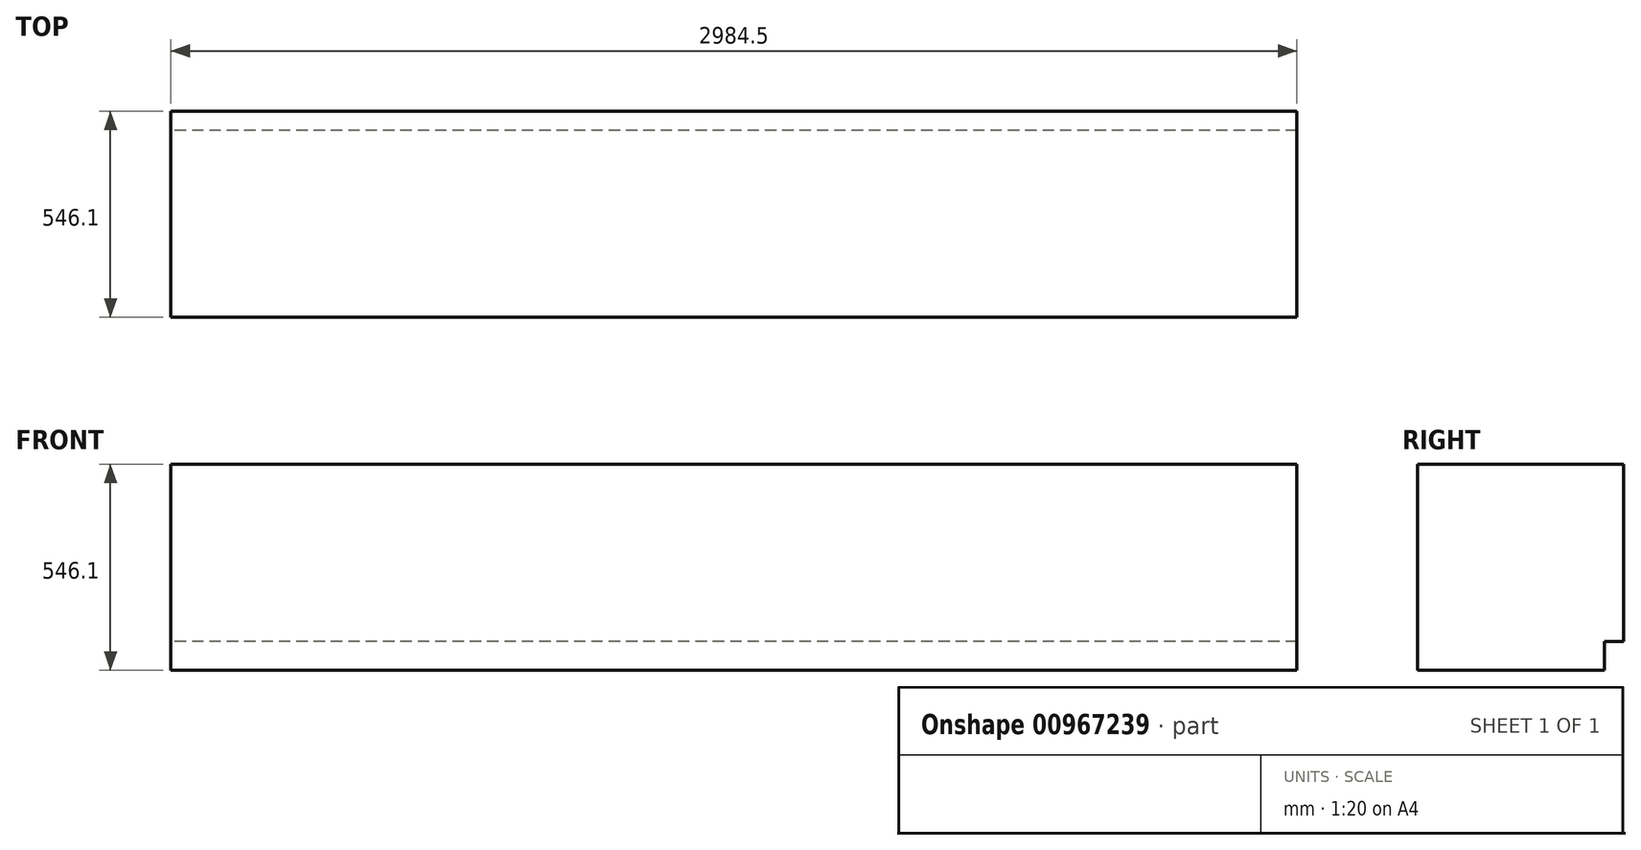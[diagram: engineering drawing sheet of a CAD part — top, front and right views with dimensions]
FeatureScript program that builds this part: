
annotation { "Feature Type Name" : "Feature", "Feature Type Description" : "" }
export const myFeature = defineFeature(function(context is Context, id is Id, definition is map)
    precondition{}
    {
        {
            var Q0;
            Q0=qCreatedBy(makeId("Front.planeOp"),FACE);
            var sketch = newSketch(context, id + "F0", { "sketchPlane" : qUnion([Q0])});
            skLineSegment(sketch, "E0.bottom", {"start": v(0, 0) * mm, "end": v(2959.1, 0) * mm, "construction": true});
            skLineSegment(sketch, "E0.left", {"start": v(0, 0) * mm, "end": v(0, 1320.8) * mm, "construction": true});
            skLineSegment(sketch, "E0.right", {"start": v(2959.1, 0) * mm, "end": v(2959.1, 1320.8) * mm, "construction": true});
            skLineSegment(sketch, "E1.bottom", {"start": v(0, 1320.8) * mm, "end": v(2959.1, 1320.8) * mm, "construction": true});
            skLineSegment(sketch, "E1.top", {"start": v(0, 1955.8) * mm, "end": v(2959.1, 1955.8) * mm, "construction": true});
            skLineSegment(sketch, "E1.left", {"start": v(0, 1320.8) * mm, "end": v(0, 1955.8) * mm, "construction": true});
            skLineSegment(sketch, "E1.right", {"start": v(2959.1, 1320.8) * mm, "end": v(2959.1, 1955.8) * mm, "construction": true});
            skLineSegment(sketch, "E2.bottom", {"start": v(0, 0) * mm, "end": v(2959.1, 0) * mm});
            skLineSegment(sketch, "E2.top", {"start": v(0, 546.1) * mm, "end": v(2959.1, 546.1) * mm});
            skLineSegment(sketch, "E2.left", {"start": v(0, 0) * mm, "end": v(0, 546.1) * mm});
            skLineSegment(sketch, "E2.right", {"start": v(2959.1, 0) * mm, "end": v(2959.1, 546.1) * mm});
            skSolve(sketch);
        }
        {
            var Q0;
            Q0=qCreatedBy(makeId("Right.planeOp"),FACE);
            var sketch = newSketch(context, id + "F1", { "sketchPlane" : qUnion([Q0])});
            skLineSegment(sketch, "E3", {"start": v(0, 0) * mm, "end": v(495.3, 0) * mm});
            skLineSegment(sketch, "E4", {"start": v(0, 0) * mm, "end": v(0, 546.1) * mm});
            skLineSegment(sketch, "E5", {"start": v(0, 546.1) * mm, "end": v(546.1, 546.1) * mm});
            skLineSegment(sketch, "E6", {"start": v(546.1, 546.1) * mm, "end": v(546.1, 76.2) * mm});
            skLineSegment(sketch, "E7", {"start": v(546.1, 76.2) * mm, "end": v(495.3, 76.2) * mm});
            skLineSegment(sketch, "E8", {"start": v(495.3, 0) * mm, "end": v(495.3, 76.2) * mm});
            skSolve(sketch);
        }
        {
            var Q0;
            Q0=makeQuery(id+"F1.imprint","IMPRINT",FACE,{"disambiguationData":[TD([[makeQuery(id+"F1.imprint","IMPRINT",EDGE,{"derivedFrom":sQuery(id+"F1.wireOp",EDGE,"E3")}),1.0]])]});
            extrude(context, id + "F2", {"entities" : qUnion([Q0]), "depth" : 2959.1 * mm, "offsetDistance" : 25.4 * mm, "hasSecondDirection" : true, "secondDirectionOppositeDirection" : true, "secondDirectionDepth" : 25.4 * mm});
        }
    });
